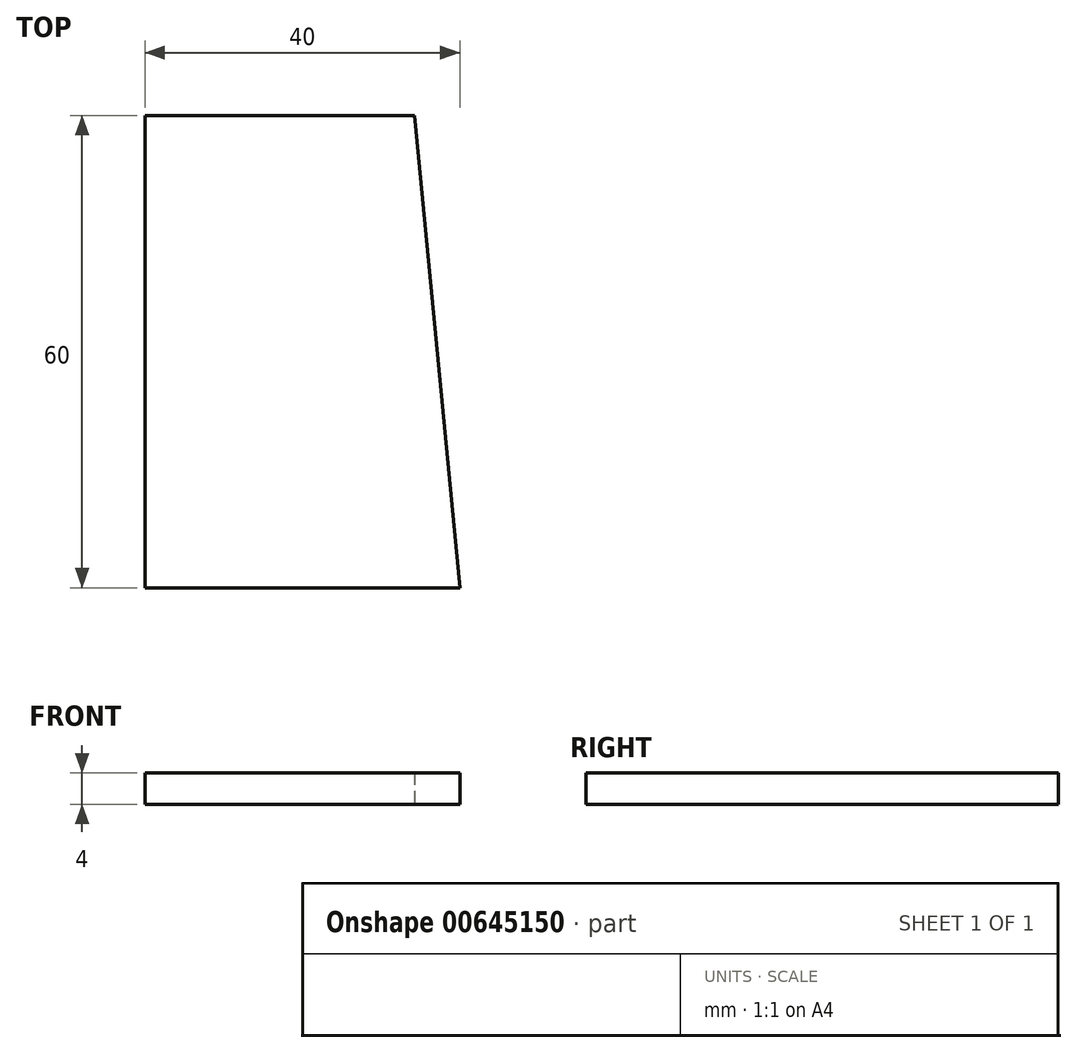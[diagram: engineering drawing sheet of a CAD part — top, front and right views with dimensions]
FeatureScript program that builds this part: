
annotation { "Feature Type Name" : "Feature", "Feature Type Description" : "" }
export const myFeature = defineFeature(function(context is Context, id is Id, definition is map)
    precondition{}
    {
        {
            var Q0;
            Q0=qCreatedBy(makeId("Top.planeOp"),FACE);
            var sketch = newSketch(context, id + "F0", { "sketchPlane" : qUnion([Q0])});
            skLineSegment(sketch, "E0.bottom", {"start": v(0, 0) * mm, "end": v(40, 0) * mm});
            skLineSegment(sketch, "E0.top", {"start": v(0, 60) * mm, "end": v(40, 60) * mm});
            skLineSegment(sketch, "E0.left", {"start": v(0, 0) * mm, "end": v(0, 60) * mm});
            skLineSegment(sketch, "E0.right", {"start": v(40, 0) * mm, "end": v(40, 60) * mm});
            skLineSegment(sketch, "E1", {"start": v(40, 0) * mm, "end": v(33.15, 71.18) * mm});
            skSolve(sketch);
        }
        {
            var Q0;
            {var subQ0=sQuery(id+"F0.wireOp",EDGE,"E0.bottom");Q0=makeQuery(id+"F0.imprint","IMPRINT",FACE,{"disambiguationData":[TD([[makeQuery(id+"F0.imprint","IMPRINT",EDGE,{"derivedFrom":subQ0}),1.0]])]});}
            extrude(context, id + "F1", {"entities" : qUnion([Q0]), "depth" : 4 * mm, "offsetDistance" : 25 * mm});
        }
    });
